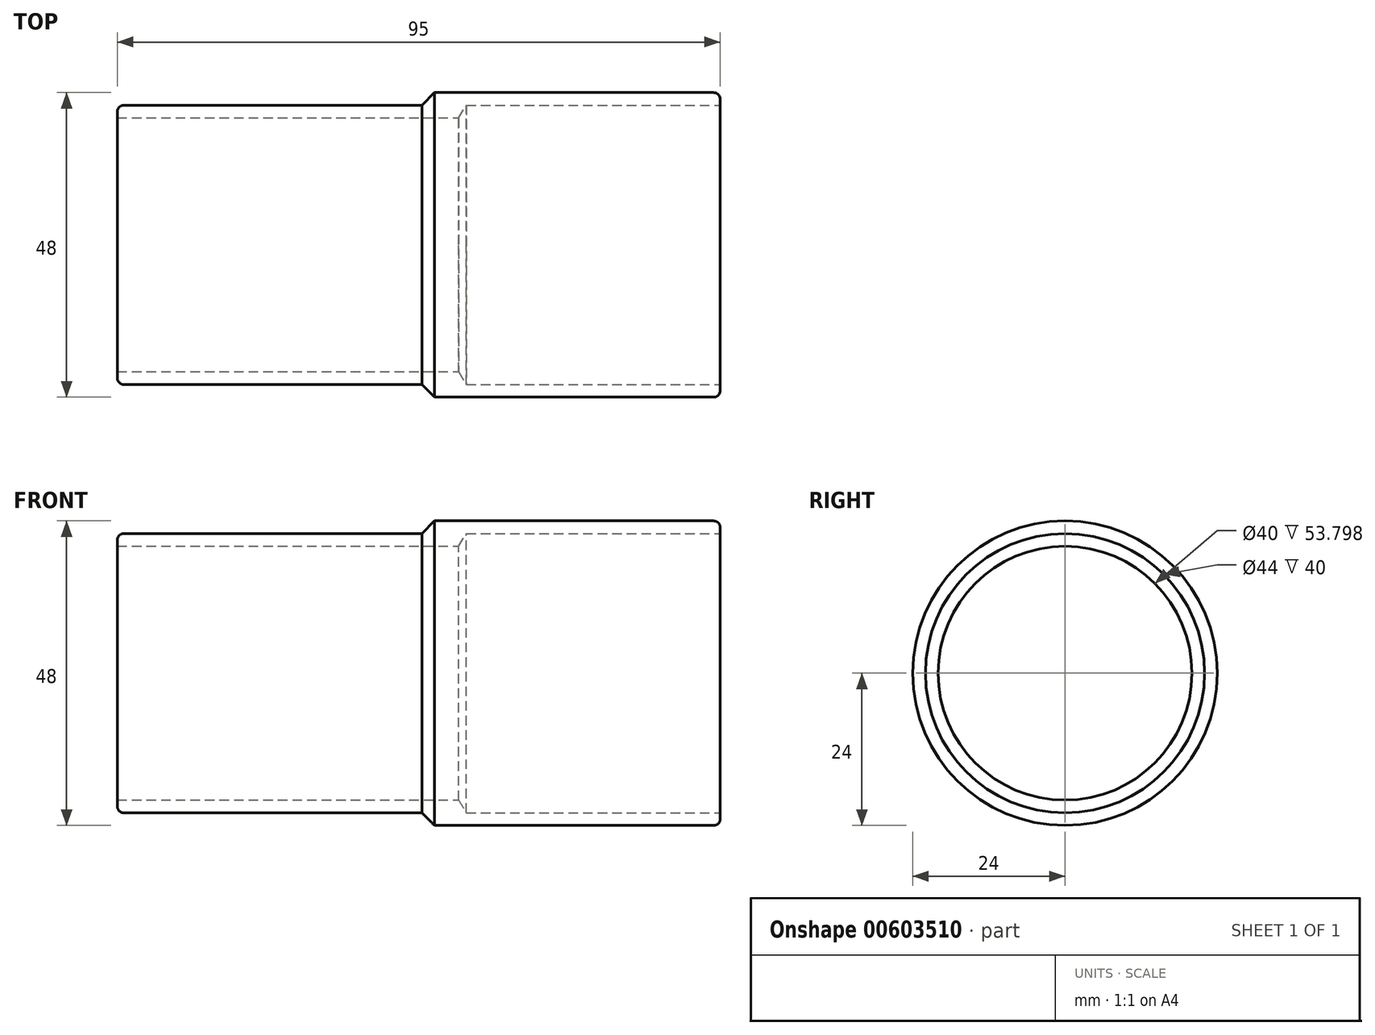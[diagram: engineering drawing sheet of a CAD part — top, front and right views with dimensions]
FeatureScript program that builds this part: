
annotation { "Feature Type Name" : "Feature", "Feature Type Description" : "" }
export const myFeature = defineFeature(function(context is Context, id is Id, definition is map)
    precondition{}
    {
        {
            var Q0;
            Q0=qCreatedBy(makeId("Front.planeOp"),FACE);
            var sketch = newSketch(context, id + "F0", { "sketchPlane" : qUnion([Q0])});
            skLineSegment(sketch, "E0", {"start": v(-95, 22) * mm, "end": v(-45, 22) * mm});
            skLineSegment(sketch, "E1", {"start": v(-45, 22) * mm, "end": v(-45, 24) * mm});
            skLineSegment(sketch, "E2", {"start": v(-45, 24) * mm, "end": v(0, 24) * mm});
            skLineSegment(sketch, "E3", {"start": v(-40, 22) * mm, "end": v(-41.2, 20) * mm});
            skLineSegment(sketch, "E4", {"start": v(-41.2, 20) * mm, "end": v(-95, 20) * mm});
            skLineSegment(sketch, "E5", {"start": v(-95, 20) * mm, "end": v(-95, 22) * mm});
            skLineSegment(sketch, "E6", {"start": v(-40, 22) * mm, "end": v(0, 22) * mm});
            skLineSegment(sketch, "E7", {"start": v(0, 22) * mm, "end": v(0, 24) * mm});
            skLineSegment(sketch, "E8", {"start": v(1.17, 0) * mm, "end": v(-119.83, 0) * mm});
            skSolve(sketch);
        }
        {
            var Q0;
            Q0 = qSketchRegion(id + "F0", true);
            var Q1;
            Q1=sQuery(id+"F0.wireOp",EDGE,"E8");
            revolve(context, id + "F1", {"entities" : qUnion([Q0]), "axis" : qUnion([Q1]), "revolveType" : RevolveType.FULL});
        }
        {
            var Q0;
            Q0=makeQuery(id+"F1.opRevolve","SWEPT_EDGE",EDGE,{"disambiguationData":[OSD([sQuery(id+"F0.wireOp",EDGE,"E0"),sQuery(id+"F0.wireOp",EDGE,"E1")])]});
            chamfer(context, id + "F2", {"entities" : qUnion([Q0]), "width" : 2 * mm, "tangentPropagation" : true});
        }
        {
            var Q0;
            Q0=makeQuery(id+"F1.opRevolve","SWEPT_EDGE",EDGE,{"disambiguationData":[OSD([sQuery(id+"F0.wireOp",EDGE,"E2"),sQuery(id+"F0.wireOp",EDGE,"E7")])]});
            var Q1;
            Q1=makeQuery(id+"F1.opRevolve","SWEPT_EDGE",EDGE,{"disambiguationData":[OSD([sQuery(id+"F0.wireOp",EDGE,"E0"),sQuery(id+"F0.wireOp",EDGE,"E5")])]});
            fillet(context, id + "F3", {"entities" : qUnion([Q0, Q1]), "radius" : 1 * mm, "tangentPropagation" : true, "allowEdgeOverflow" : false});
        }
    });
